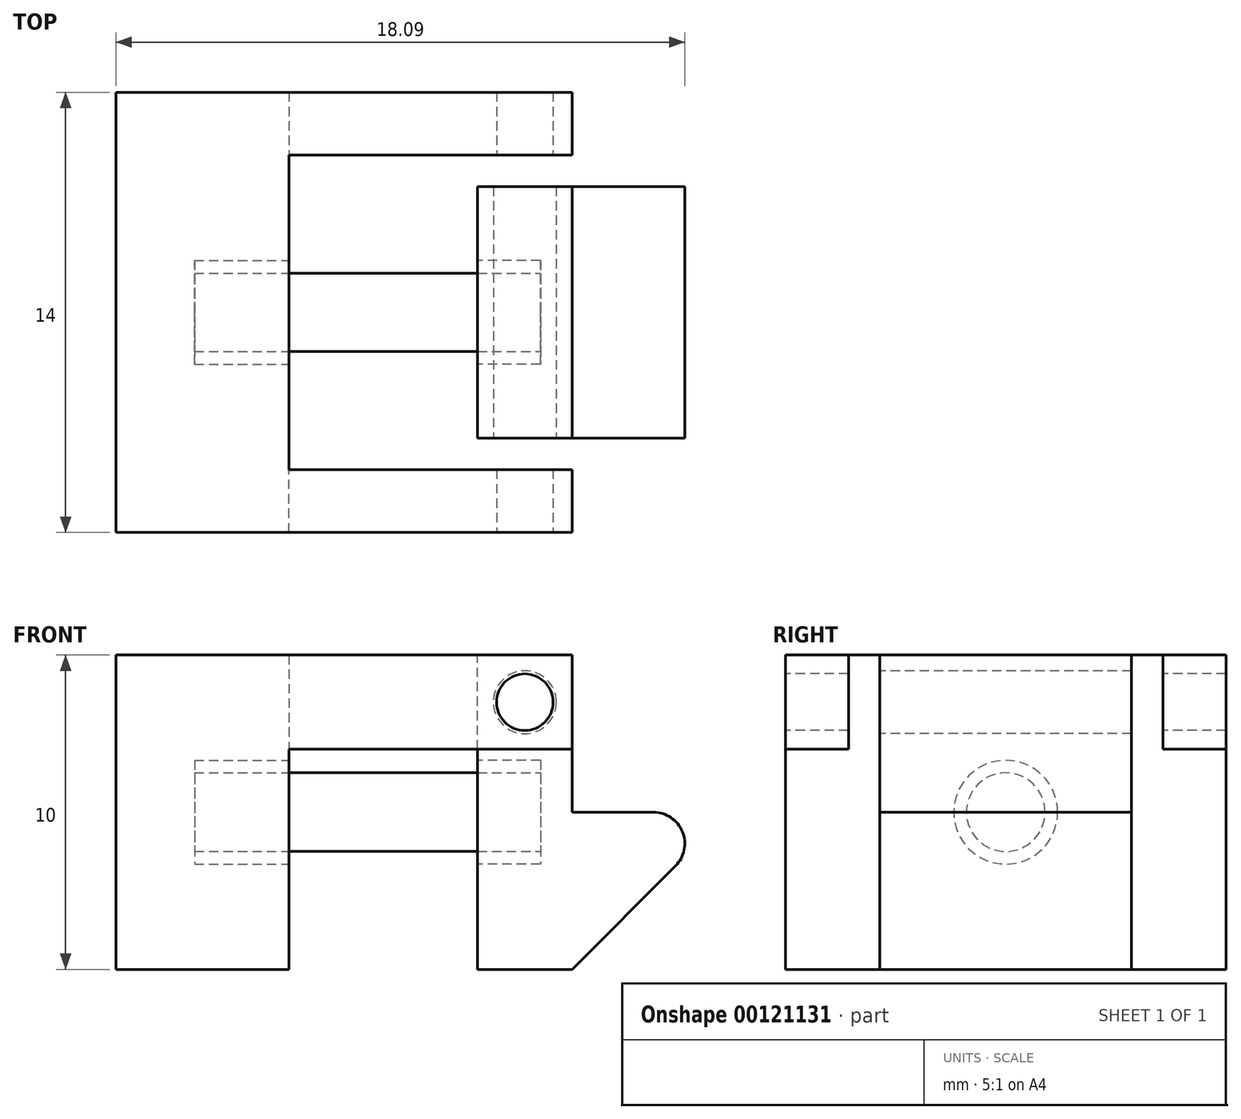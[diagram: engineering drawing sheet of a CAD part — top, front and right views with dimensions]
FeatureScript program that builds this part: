
annotation { "Feature Type Name" : "Feature", "Feature Type Description" : "" }
export const myFeature = defineFeature(function(context is Context, id is Id, definition is map)
    precondition{}
    {
        {
            var Q0;
            Q0=qCreatedBy(makeId("Front.planeOp"),FACE);
            var sketch = newSketch(context, id + "F0", { "sketchPlane" : qUnion([Q0])});
            skLineSegment(sketch, "E0", {"start": v(0, 0) * mm, "end": v(0, 10) * mm});
            skLineSegment(sketch, "E1", {"start": v(0, 10) * mm, "end": v(3, 10) * mm});
            skLineSegment(sketch, "E2", {"start": v(3, 10) * mm, "end": v(3, 5) * mm});
            skLineSegment(sketch, "E3", {"start": v(3, 5) * mm, "end": v(5.59, 5) * mm});
            skLineSegment(sketch, "E4", {"start": v(3, 5) * mm, "end": v(3, 0) * mm, "construction": true});
            skLineSegment(sketch, "E5", {"start": v(3, 0) * mm, "end": v(6.3, 3.3) * mm});
            skLineSegment(sketch, "E6", {"start": v(0, 0) * mm, "end": v(3, 0) * mm});
            skPoint(sketch, "E7.visualSharp", {"position": v(8, 5) * mm});
            skArc(sketch, "E7.filletArc", {"start": v(6.3, 3.3) * mm, "mid": v(6.5, 4.38) * mm, "end": v(5.59, 5) * mm});
            skSolve(sketch);
        }
        {
            var Q0;
            Q0 = qSketchRegion(id + "F0", true);
            extrude(context, id + "F1", {"entities" : qUnion([Q0]), "depth" : 8 * mm});
        }
        {
            var Q0;
            Q0=makeQuery(id+"F1.opExtrude","CAP_FACE",FACE,{"disambiguationData":[OSD([sQuery(id+"F0.wireOp",EDGE,"E0"),sQuery(id+"F0.wireOp",EDGE,"E1"),sQuery(id+"F0.wireOp",EDGE,"E2"),sQuery(id+"F0.wireOp",EDGE,"E3"),sQuery(id+"F0.wireOp",EDGE,"E5"),sQuery(id+"F0.wireOp",EDGE,"E6"),sQuery(id+"F0.wireOp",EDGE,"E7.filletArc")])],"isStart":false});
            var sketch = newSketch(context, id + "F2", { "sketchPlane" : qUnion([Q0])});
            skLineSegment(sketch, "E8", {"start": v(0, 10) * mm, "end": v(1.5, 10) * mm, "construction": true});
            skLineSegment(sketch, "E9", {"start": v(1.5, 10) * mm, "end": v(1.5, 8.5) * mm, "construction": true});
            skCircle(sketch, "E10", {"center": v(1.5, 8.5) * mm, "radius": 1 * mm});
            skSolve(sketch);
        }
        {
            var Q0;
            Q0 = qSketchRegion(id + "F2", true);
            extrude(context, id + "F3", {"entities" : qUnion([Q0]), "operationType" : NewBodyOperationType.REMOVE, "endBound" : BoundingType.THROUGH_ALL, "oppositeDirection" : true, "depth" : 25 * mm});
        }
        {
            var Q0;
            Q0=makeQuery(id+"F1.opExtrude","SWEPT_FACE",FACE,{"disambiguationData":[OSD([sQuery(id+"F0.wireOp",EDGE,"E0")])]});
            var sketch = newSketch(context, id + "F4", { "sketchPlane" : qUnion([Q0])});
            skLineSegment(sketch, "E11", {"start": v(0, 0) * mm, "end": v(4, 0) * mm, "construction": true});
            skLineSegment(sketch, "E12", {"start": v(4, 0) * mm, "end": v(4, 5) * mm, "construction": true});
            skCircle(sketch, "E13", {"center": v(4, 5) * mm, "radius": 1.65 * mm});
            skSolve(sketch);
        }
        {
            var Q0;
            Q0=makeQuery(id+"F4.imprint","IMPRINT",FACE,{"disambiguationData":[TD([[makeQuery(id+"F4.imprint","IMPRINT",EDGE,{"derivedFrom":sQuery(id+"F4.wireOp",EDGE,"E13")}),1.0]])]});
            extrude(context, id + "F5", {"entities" : qUnion([Q0]), "operationType" : NewBodyOperationType.REMOVE, "oppositeDirection" : true, "depth" : 2 * mm});
        }
        {
            var Q0;
            Q0=makeQuery(id+"F5.boolean.opBoolean","COPY",FACE,{"derivedFrom":makeQuery(id+"F5.opExtrude","CAP_FACE",FACE,{"disambiguationData":[OSD([sQuery(id+"F4.wireOp",EDGE,"E13")])],"isStart":false})});
            var sketch = newSketch(context, id + "F6", { "sketchPlane" : qUnion([Q0])});
            skLineSegment(sketch, "E14", {"start": v(4.04, 6.65) * mm, "end": v(4, 5) * mm, "construction": true});
            skCircle(sketch, "E15", {"center": v(4, 5) * mm, "radius": 1.25 * mm});
            skSolve(sketch);
        }
        {
            var Q0;
            Q0 = qSketchRegion(id + "F6", true);
            extrude(context, id + "F7", {"entities" : qUnion([Q0]), "depth" : 8 * mm});
        }
        {
            var Q0;
            Q0=makeQuery(id+"F1.opExtrude","CAP_FACE",FACE,{"disambiguationData":[OSD([sQuery(id+"F0.wireOp",EDGE,"E0"),sQuery(id+"F0.wireOp",EDGE,"E1"),sQuery(id+"F0.wireOp",EDGE,"E2"),sQuery(id+"F0.wireOp",EDGE,"E3"),sQuery(id+"F0.wireOp",EDGE,"E5"),sQuery(id+"F0.wireOp",EDGE,"E6"),sQuery(id+"F0.wireOp",EDGE,"E7.filletArc")])],"isStart":true});
            var sketch = newSketch(context, id + "F8", { "sketchPlane" : qUnion([Q0])});
            skCircle(sketch, "E16", {"center": v(-1.5, 8.5) * mm, "radius": 0.9 * mm});
            skSolve(sketch);
        }
        {
            var Q0;
            Q0 = qSketchRegion(id + "F8", true);
            extrude(context, id + "F9", {"entities" : qUnion([Q0]), "depth" : 1 * mm, "hasSecondDirection" : true, "secondDirectionOppositeDirection" : true, "secondDirectionDepth" : 9 * mm});
        }
        {
            var Q0;
            Q0=makeQuery(id+"F9.opExtrude","CAP_FACE",FACE,{"disambiguationData":[OSD([sQuery(id+"F8.wireOp",EDGE,"E16")])],"isStart":true});
            var sketch = newSketch(context, id + "F10", { "sketchPlane" : qUnion([Q0])});
            skLineSegment(sketch, "E17", {"start": v(1.5, 8.5) * mm, "end": v(1.5, 10) * mm, "construction": true});
            skLineSegment(sketch, "E18", {"start": v(1.5, 10) * mm, "end": v(-10.5, 10) * mm});
            skLineSegment(sketch, "E19", {"start": v(1.5, 10) * mm, "end": v(3, 10) * mm});
            skLineSegment(sketch, "E20", {"start": v(3, 10) * mm, "end": v(3, 7) * mm});
            skLineSegment(sketch, "E21", {"start": v(3, 7) * mm, "end": v(-10.5, 7) * mm});
            skLineSegment(sketch, "E22", {"start": v(-10.5, 10) * mm, "end": v(-10.5, 7) * mm});
            skSolve(sketch);
        }
        {
            var Q0;
            Q0 = qSketchRegion(id + "F10", true);
            extrude(context, id + "F11", {"entities" : qUnion([Q0]), "operationType" : NewBodyOperationType.ADD, "depth" : 2 * mm});
        }
        {
            var Q0;
            Q0=makeQuery(id+"F9.opExtrude","CAP_FACE",FACE,{"disambiguationData":[OSD([sQuery(id+"F8.wireOp",EDGE,"E16")])],"isStart":false});
            var sketch = newSketch(context, id + "F12", { "sketchPlane" : qUnion([Q0])});
            skLineSegment(sketch, "E23", {"start": v(-1.5, 8.5) * mm, "end": v(-1.5, 10) * mm, "construction": true});
            skLineSegment(sketch, "E24", {"start": v(-1.5, 10) * mm, "end": v(-3, 10) * mm, "construction": true});
            skLineSegment(sketch, "E25.bottom", {"start": v(-3, 10) * mm, "end": v(10.5, 10) * mm});
            skLineSegment(sketch, "E25.top", {"start": v(-3, 7) * mm, "end": v(10.5, 7) * mm});
            skLineSegment(sketch, "E25.left", {"start": v(-3, 10) * mm, "end": v(-3, 7) * mm});
            skLineSegment(sketch, "E25.right", {"start": v(10.5, 10) * mm, "end": v(10.5, 7) * mm});
            skSolve(sketch);
        }
        {
            var Q0;
            Q0 = qSketchRegion(id + "F12", true);
            extrude(context, id + "F13", {"entities" : qUnion([Q0]), "operationType" : NewBodyOperationType.ADD, "depth" : 2 * mm});
        }
        {
            var Q0;
            Q0=makeQuery(id+"F13.opExtrude","SWEPT_FACE",FACE,{"disambiguationData":[OSD([sQuery(id+"F12.wireOp",EDGE,"E25.right")])]});
            var sketch = newSketch(context, id + "F14", { "sketchPlane" : qUnion([Q0])});
            skLineSegment(sketch, "E26.bottom", {"start": v(-3, 10) * mm, "end": v(11, 10) * mm});
            skLineSegment(sketch, "E26.top", {"start": v(-3, 0) * mm, "end": v(11, 0) * mm});
            skLineSegment(sketch, "E26.left", {"start": v(-3, 10) * mm, "end": v(-3, 0) * mm});
            skLineSegment(sketch, "E26.right", {"start": v(11, 10) * mm, "end": v(11, 0) * mm});
            skSolve(sketch);
        }
        {
            var Q0;
            Q0 = qSketchRegion(id + "F14", true);
            var Q1;
            Q1=makeQuery(id+"F7.opExtrude","CAP_FACE",FACE,{"disambiguationData":[OSD([sQuery(id+"F6.wireOp",EDGE,"E15")])],"isStart":false});
            extrude(context, id + "F15", {"entities" : qUnion([Q0]), "depth" : 1 * mm, "hasSecondDirection" : true, "secondDirectionBound" : SecondDirectionBoundingType.UP_TO_SURFACE, "secondDirectionOppositeDirection" : true, "secondDirectionBoundEntityFace" : qUnion([Q1]), "secondDirectionDepth" : 25 * mm});
        }
        {
            var Q0;
            Q0=makeQuery(id+"F9.opExtrude","SWEPT_BODY",BODY,{"disambiguationData":[OSD([sQuery(id+"F8.wireOp",EDGE,"E16")])]});
            var Q1;
            Q1=makeQuery(id+"F15.opExtrude","SWEPT_BODY",BODY,{"disambiguationData":[OSD([sQuery(id+"F14.wireOp",EDGE,"E26.bottom"),sQuery(id+"F14.wireOp",EDGE,"E26.top"),sQuery(id+"F14.wireOp",EDGE,"E26.left"),sQuery(id+"F14.wireOp",EDGE,"E26.right")])]});
            booleanBodies(context, id + "F16", {"operationType" : BooleanOperationType.UNION, "tools" : qUnion([Q0, Q1])});
        }
        {
            var Q0;
            Q0=makeQuery(id+"F7.opExtrude","CAP_FACE",FACE,{"disambiguationData":[OSD([sQuery(id+"F6.wireOp",EDGE,"E15")])],"isStart":false});
            var sketch = newSketch(context, id + "F17", { "sketchPlane" : qUnion([Q0])});
            skCircle(sketch, "E27", {"center": v(4, 5) * mm, "radius": 1.65 * mm});
            skSolve(sketch);
        }
        {
            var Q0;
            Q0 = qSketchRegion(id + "F17", true);
            extrude(context, id + "F18", {"entities" : qUnion([Q0]), "depth" : 3 * mm});
        }
        {
            var Q0;
            Q0=makeQuery(id+"F18.opExtrude","SWEPT_BODY",BODY,{"disambiguationData":[OSD([sQuery(id+"F17.wireOp",EDGE,"E27")])]});
            var Q1;
            Q1=makeQuery(id+"F9.opExtrude","SWEPT_BODY",BODY,{"disambiguationData":[OSD([sQuery(id+"F8.wireOp",EDGE,"E16")])]});
            booleanBodies(context, id + "F19", {"operationType" : BooleanOperationType.SUBTRACTION, "tools" : qUnion([Q0]), "targets" : qUnion([Q1])});
        }
        {
            var Q0;
            Q0=makeQuery(id+"F7.opExtrude","CAP_FACE",FACE,{"disambiguationData":[OSD([sQuery(id+"F6.wireOp",EDGE,"E15")])],"isStart":false});
            extrude(context, id + "F20", {"entities" : qUnion([Q0]), "operationType" : NewBodyOperationType.ADD, "depth" : 3 * mm});
        }
        {
            var Q0;
            Q0=makeQuery(id+"F16.opBoolean","MERGE",FACE,{"derivedFrom":[makeQuery(id+"F11.opExtrude","CAP_FACE",FACE,{"disambiguationData":[OSD([sQuery(id+"F10.wireOp",EDGE,"E18"),sQuery(id+"F10.wireOp",EDGE,"E19"),sQuery(id+"F10.wireOp",EDGE,"E20"),sQuery(id+"F10.wireOp",EDGE,"E21"),sQuery(id+"F10.wireOp",EDGE,"E22")])],"isStart":false}),makeQuery(id+"F15.opExtrude","SWEPT_FACE",FACE,{"disambiguationData":[OSD([sQuery(id+"F14.wireOp",EDGE,"E26.right")])]})]});
            var sketch = newSketch(context, id + "F21", { "sketchPlane" : qUnion([Q0])});
            skLineSegment(sketch, "E28", {"start": v(3, 10) * mm, "end": v(1.5, 10) * mm, "construction": true});
            skLineSegment(sketch, "E29", {"start": v(1.5, 10) * mm, "end": v(1.5, 8.5) * mm, "construction": true});
            skCircle(sketch, "E30", {"center": v(1.5, 8.5) * mm, "radius": 0.9 * mm});
            skSolve(sketch);
        }
        {
            var Q0;
            Q0 = qSketchRegion(id + "F21", true);
            extrude(context, id + "F22", {"entities" : qUnion([Q0]), "operationType" : NewBodyOperationType.REMOVE, "endBound" : BoundingType.THROUGH_ALL, "oppositeDirection" : true, "depth" : 25 * mm});
        }
    });
